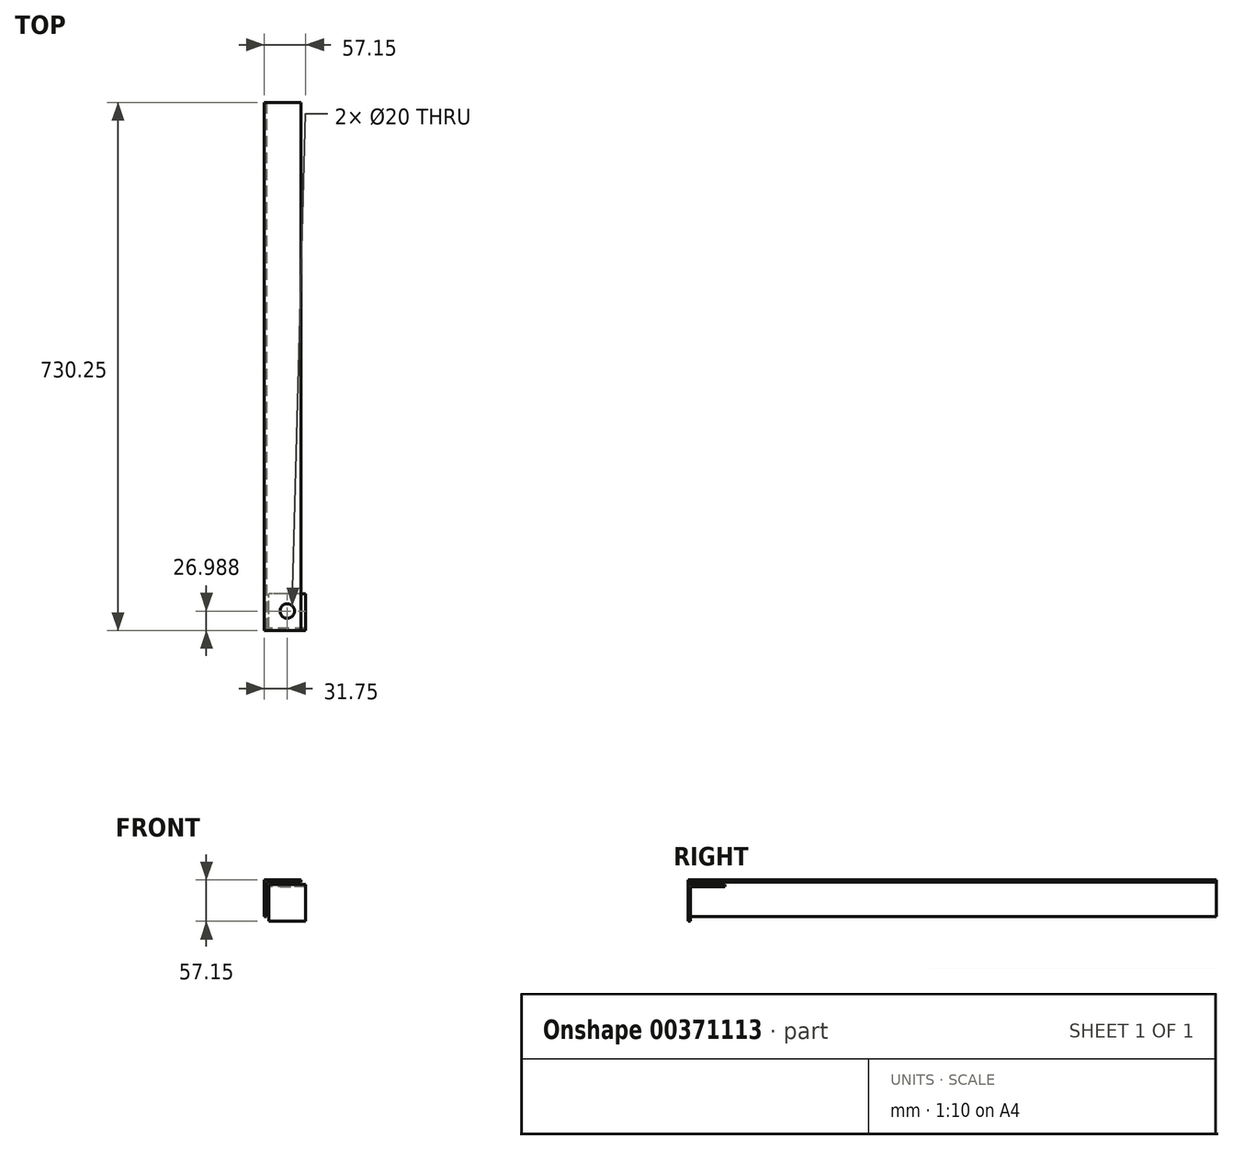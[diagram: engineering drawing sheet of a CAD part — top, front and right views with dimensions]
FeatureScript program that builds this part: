
annotation { "Feature Type Name" : "Feature", "Feature Type Description" : "" }
export const myFeature = defineFeature(function(context is Context, id is Id, definition is map)
    precondition{}
    {
        {
            var Q0;
            Q0=qCreatedBy(makeId("Right.planeOp"),FACE);
            var sketch = newSketch(context, id + "F0", { "sketchPlane" : qUnion([Q0])});
            skLineSegment(sketch, "E0.top", {"start": v(0, 50.8) * mm, "end": v(50.8, 50.8) * mm});
            skLineSegment(sketch, "E0.left", {"start": v(0, 0) * mm, "end": v(0, 50.8) * mm});
            skLineSegment(sketch, "E1.right", {"start": v(3.17, 0) * mm, "end": v(3.17, 47.63) * mm});
            skLineSegment(sketch, "E2", {"start": v(3.17, 0) * mm, "end": v(0, 0) * mm});
            skLineSegment(sketch, "E3", {"start": v(3.17, 47.63) * mm, "end": v(50.8, 47.63) * mm});
            skLineSegment(sketch, "E4", {"start": v(50.8, 47.63) * mm, "end": v(50.8, 50.8) * mm});
            skSolve(sketch);
        }
        {
            var Q0;
            Q0 = qSketchRegion(id + "F0", true);
            extrude(context, id + "F1", {"entities" : qUnion([Q0]), "depth" : 50.8 * mm});
        }
        {
            var Q0;
            Q0=qCreatedBy(makeId("Front.planeOp"),FACE);
            var sketch = newSketch(context, id + "F2", { "sketchPlane" : qUnion([Q0])});
            skLineSegment(sketch, "E5.top", {"start": v(-6.35, 57.15) * mm, "end": v(44.45, 57.15) * mm});
            skLineSegment(sketch, "E5.left", {"start": v(-6.35, 6.35) * mm, "end": v(-6.35, 57.15) * mm});
            skLineSegment(sketch, "E6.right", {"start": v(-3.18, 6.35) * mm, "end": v(-3.18, 53.98) * mm});
            skLineSegment(sketch, "E7", {"start": v(-3.18, 6.35) * mm, "end": v(-6.35, 6.35) * mm});
            skLineSegment(sketch, "E8", {"start": v(-3.17, 53.98) * mm, "end": v(44.45, 53.98) * mm});
            skLineSegment(sketch, "E9", {"start": v(44.45, 53.98) * mm, "end": v(44.45, 57.15) * mm});
            skSolve(sketch);
        }
        {
            var Q0;
            Q0 = qSketchRegion(id + "F2", true);
            extrude(context, id + "F3", {"entities" : qUnion([Q0]), "oppositeDirection" : true, "depth" : 730.25 * mm});
        }
        {
            var Q0;
            Q0=makeQuery(id+"F1.opExtrude","SWEPT_FACE",FACE,{"disambiguationData":[OSD([sQuery(id+"F0.wireOp",EDGE,"E3")])]});
            var sketch = newSketch(context, id + "F4", { "sketchPlane" : qUnion([Q0])});
            skCircle(sketch, "E10", {"center": v(25.4, -26.99) * mm, "radius": 10 * mm});
            skPoint(sketch, "E10.centerSnap0", {"position": v(25.4, -50.8) * mm});
            skPoint(sketch, "E10.centerSnap1", {"position": v(0, -26.99) * mm});
            skSolve(sketch);
        }
        {
            var Q0;
            Q0 = qSketchRegion(id + "F4", true);
            extrude(context, id + "F5", {"entities" : qUnion([Q0]), "operationType" : NewBodyOperationType.REMOVE, "endBound" : BoundingType.THROUGH_ALL, "oppositeDirection" : true, "depth" : 25.4 * mm});
        }
        {
            var Q0;
            Q0=makeQuery(id+"F3.opExtrude","CAP_FACE",FACE,{"disambiguationData":[OSD([sQuery(id+"F2.wireOp",EDGE,"E5.top"),sQuery(id+"F2.wireOp",EDGE,"E5.left"),sQuery(id+"F2.wireOp",EDGE,"E6.right"),sQuery(id+"F2.wireOp",EDGE,"E7"),sQuery(id+"F2.wireOp",EDGE,"E8"),sQuery(id+"F2.wireOp",EDGE,"E9")])],"isStart":true});
            var Q1;
            Q1=makeQuery(id+"F3.opExtrude","CAP_FACE",FACE,{"disambiguationData":[OSD([sQuery(id+"F2.wireOp",EDGE,"E5.top"),sQuery(id+"F2.wireOp",EDGE,"E5.left"),sQuery(id+"F2.wireOp",EDGE,"E6.right"),sQuery(id+"F2.wireOp",EDGE,"E7"),sQuery(id+"F2.wireOp",EDGE,"E8"),sQuery(id+"F2.wireOp",EDGE,"E9")])],"isStart":false});
            cPlane(context, id + "F6", {"entities" : qUnion([Q0, Q1]), "cplaneType" : CPlaneType.MID_PLANE, "offset" : 25.4 * mm, "width" : 152.4 * mm, "height" : 152.4 * mm});
        }
    });
